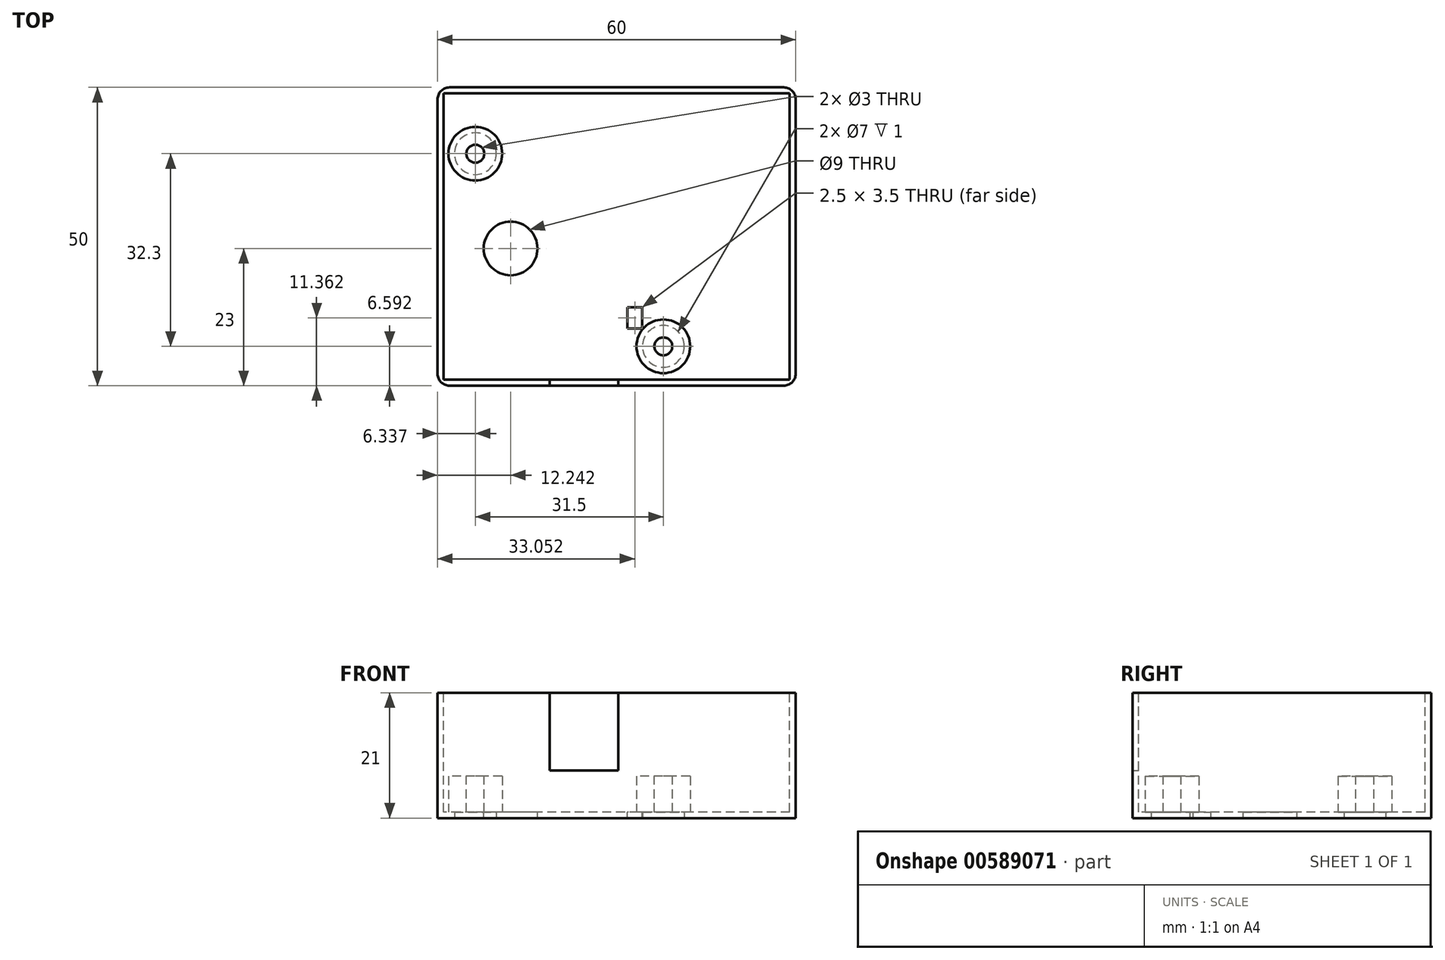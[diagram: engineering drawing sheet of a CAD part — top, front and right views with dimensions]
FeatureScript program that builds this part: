
annotation { "Feature Type Name" : "Feature", "Feature Type Description" : "" }
export const myFeature = defineFeature(function(context is Context, id is Id, definition is map)
    precondition{}
    {
        {
            var Q0;
            Q0=qCreatedBy(makeId("Top.planeOp"),FACE);
            var sketch = newSketch(context, id + "F0", { "sketchPlane" : qUnion([Q0])});
            skLineSegment(sketch, "E0.bottom", {"start": v(-60, 50) * mm, "end": v(0, 50) * mm});
            skLineSegment(sketch, "E0.top", {"start": v(-60, 0) * mm, "end": v(0, 0) * mm});
            skLineSegment(sketch, "E0.left", {"start": v(-60, 50) * mm, "end": v(-60, 0) * mm});
            skLineSegment(sketch, "E0.right", {"start": v(0, 50) * mm, "end": v(0, 0) * mm});
            skSolve(sketch);
        }
        {
            var Q0;
            Q0=makeQuery(id+"F0.imprint","IMPRINT",FACE,{"disambiguationData":[TD([[makeQuery(id+"F0.imprint","IMPRINT",EDGE,{"derivedFrom":sQuery(id+"F0.wireOp",EDGE,"E0.bottom")}),-1.0]])]});
            extrude(context, id + "F1", {"entities" : qUnion([Q0]), "depth" : 21 * mm, "offsetDistance" : 25 * mm});
        }
        {
            var Q0;
            Q0=makeQuery(id+"F1.opExtrude","CAP_FACE",FACE,{"disambiguationData":[OSD([sQuery(id+"F0.wireOp",EDGE,"E0.bottom"),sQuery(id+"F0.wireOp",EDGE,"E0.top"),sQuery(id+"F0.wireOp",EDGE,"E0.left"),sQuery(id+"F0.wireOp",EDGE,"E0.right")])],"isStart":false});
            var sketch = newSketch(context, id + "F2", { "sketchPlane" : qUnion([Q0])});
            skLineSegment(sketch, "E1.bottom", {"start": v(-1, 49) * mm, "end": v(-59, 49) * mm});
            skLineSegment(sketch, "E1.top", {"start": v(-1, 1) * mm, "end": v(-59, 1) * mm});
            skLineSegment(sketch, "E1.left", {"start": v(-1, 49) * mm, "end": v(-1, 1) * mm});
            skLineSegment(sketch, "E1.right", {"start": v(-59, 49) * mm, "end": v(-59, 1) * mm});
            skPoint(sketch, "E1.middle", {"position": v(-30, 25) * mm});
            skPoint(sketch, "E1.middle.positionSnap0", {"position": v(-60, 25) * mm});
            skPoint(sketch, "E1.middle.positionSnap1", {"position": v(-30, 50) * mm});
            skPoint(sketch, "E1.centerSnap0", {"position": v(-60, 25) * mm});
            skPoint(sketch, "E1.centerSnap1", {"position": v(-30, 50) * mm});
            skSolve(sketch);
        }
        {
            var Q0;
            Q0=makeQuery(id+"F2.imprint","IMPRINT",FACE,{"disambiguationData":[TD([[makeQuery(id+"F2.imprint","IMPRINT",EDGE,{"derivedFrom":sQuery(id+"F2.wireOp",EDGE,"E1.bottom")}),1.0]])]});
            extrude(context, id + "F3", {"entities" : qUnion([Q0]), "operationType" : NewBodyOperationType.REMOVE, "oppositeDirection" : true, "depth" : 20 * mm, "offsetDistance" : 25 * mm});
        }
        {
            var Q0;
            Q0=makeQuery(id+"F3.boolean.opBoolean","COPY",FACE,{"derivedFrom":makeQuery(id+"F3.opExtrude","CAP_FACE",FACE,{"disambiguationData":[OSD([sQuery(id+"F2.wireOp",EDGE,"E1.bottom"),sQuery(id+"F2.wireOp",EDGE,"E1.top"),sQuery(id+"F2.wireOp",EDGE,"E1.left"),sQuery(id+"F2.wireOp",EDGE,"E1.right")])],"isStart":false})});
            var sketch = newSketch(context, id + "F4", { "sketchPlane" : qUnion([Q0])});
            skSolve(sketch);
        }
        {
            var Q0;
            Q0=makeQuery(id+"F1.opExtrude","SWEPT_EDGE",EDGE,{"disambiguationData":[OSD([sQuery(id+"F0.wireOp",EDGE,"E0.bottom"),sQuery(id+"F0.wireOp",EDGE,"E0.left")])]});
            var Q1;
            Q1=makeQuery(id+"FCYQWNy7Zb7PqlJ_1.opExtrude","SWEPT_EDGE",EDGE,{"disambiguationData":[OSD([sQuery(id+"F0qmjPTTrngIJEc_1.wireOp",EDGE,"DvuROJ63-KSk5-jzMp-zI5F-EhPobcGynQcb.top"),sQuery(id+"F0qmjPTTrngIJEc_1.wireOp",EDGE,"DvuROJ63-KSk5-jzMp-zI5F-EhPobcGynQcb.right")])]});
            var Q2;
            Q2=makeQuery(id+"FCYQWNy7Zb7PqlJ_1.opExtrude","SWEPT_EDGE",EDGE,{"disambiguationData":[OSD([sQuery(id+"F2.wireOp",EDGE,"E1.bottom"),sQuery(id+"F0qmjPTTrngIJEc_1.wireOp",EDGE,"DvuROJ63-KSk5-jzMp-zI5F-EhPobcGynQcb.bottom"),sQuery(id+"F0qmjPTTrngIJEc_1.wireOp",EDGE,"DvuROJ63-KSk5-jzMp-zI5F-EhPobcGynQcb.right")])]});
            var Q3;
            Q3=makeQuery(id+"FCYQWNy7Zb7PqlJ_1.opExtrude","SWEPT_EDGE",EDGE,{"disambiguationData":[OSD([sQuery(id+"F2.wireOp",EDGE,"E1.right"),sQuery(id+"F0qmjPTTrngIJEc_1.wireOp",EDGE,"DvuROJ63-KSk5-jzMp-zI5F-EhPobcGynQcb.top"),sQuery(id+"F0qmjPTTrngIJEc_1.wireOp",EDGE,"DvuROJ63-KSk5-jzMp-zI5F-EhPobcGynQcb.left")])]});
            var Q4;
            Q4=makeQuery(id+"FCYQWNy7Zb7PqlJ_1.opExtrude","SWEPT_EDGE",EDGE,{"disambiguationData":[OSD([sQuery(id+"F2.wireOp",EDGE,"E1.bottom"),sQuery(id+"F0qmjPTTrngIJEc_1.wireOp",EDGE,"zE6tPnLL-G540-4zGb-CKbz-ck4JLzuL5Bhh.bottom"),sQuery(id+"F0qmjPTTrngIJEc_1.wireOp",EDGE,"zE6tPnLL-G540-4zGb-CKbz-ck4JLzuL5Bhh.right")])]});
            var Q5;
            Q5=makeQuery(id+"FCYQWNy7Zb7PqlJ_1.opExtrude","SWEPT_EDGE",EDGE,{"disambiguationData":[OSD([sQuery(id+"F0qmjPTTrngIJEc_1.wireOp",EDGE,"zE6tPnLL-G540-4zGb-CKbz-ck4JLzuL5Bhh.top"),sQuery(id+"F0qmjPTTrngIJEc_1.wireOp",EDGE,"zE6tPnLL-G540-4zGb-CKbz-ck4JLzuL5Bhh.right")])]});
            var Q6;
            Q6=makeQuery(id+"FCYQWNy7Zb7PqlJ_1.opExtrude","SWEPT_EDGE",EDGE,{"disambiguationData":[OSD([sQuery(id+"F2.wireOp",EDGE,"E1.left"),sQuery(id+"F0qmjPTTrngIJEc_1.wireOp",EDGE,"zE6tPnLL-G540-4zGb-CKbz-ck4JLzuL5Bhh.top"),sQuery(id+"F0qmjPTTrngIJEc_1.wireOp",EDGE,"zE6tPnLL-G540-4zGb-CKbz-ck4JLzuL5Bhh.left")])]});
            var Q7;
            Q7=makeQuery(id+"F1.opExtrude","SWEPT_EDGE",EDGE,{"disambiguationData":[OSD([sQuery(id+"F0.wireOp",EDGE,"E0.bottom"),sQuery(id+"F0.wireOp",EDGE,"E0.right")])]});
            var Q8;
            Q8=makeQuery(id+"FCYQWNy7Zb7PqlJ_1.opExtrude","SWEPT_EDGE",EDGE,{"disambiguationData":[OSD([sQuery(id+"F2.wireOp",EDGE,"E1.left"),sQuery(id+"F0qmjPTTrngIJEc_1.wireOp",EDGE,"89tvnpWX-ODYg-inec-HLnJ-TwMMxXkBzffX.top"),sQuery(id+"F0qmjPTTrngIJEc_1.wireOp",EDGE,"89tvnpWX-ODYg-inec-HLnJ-TwMMxXkBzffX.left")])]});
            var Q9;
            Q9=makeQuery(id+"FCYQWNy7Zb7PqlJ_1.opExtrude","SWEPT_EDGE",EDGE,{"disambiguationData":[OSD([sQuery(id+"F0qmjPTTrngIJEc_1.wireOp",EDGE,"89tvnpWX-ODYg-inec-HLnJ-TwMMxXkBzffX.top"),sQuery(id+"F0qmjPTTrngIJEc_1.wireOp",EDGE,"89tvnpWX-ODYg-inec-HLnJ-TwMMxXkBzffX.right")])]});
            var Q10;
            Q10=makeQuery(id+"FCYQWNy7Zb7PqlJ_1.opExtrude","SWEPT_EDGE",EDGE,{"disambiguationData":[OSD([sQuery(id+"F2.wireOp",EDGE,"E1.top"),sQuery(id+"F0qmjPTTrngIJEc_1.wireOp",EDGE,"89tvnpWX-ODYg-inec-HLnJ-TwMMxXkBzffX.bottom"),sQuery(id+"F0qmjPTTrngIJEc_1.wireOp",EDGE,"89tvnpWX-ODYg-inec-HLnJ-TwMMxXkBzffX.right")])]});
            var Q11;
            Q11=makeQuery(id+"F1.opExtrude","SWEPT_EDGE",EDGE,{"disambiguationData":[OSD([sQuery(id+"F0.wireOp",EDGE,"E0.top"),sQuery(id+"F0.wireOp",EDGE,"E0.right")])]});
            var Q12;
            Q12=makeQuery(id+"F1.opExtrude","SWEPT_EDGE",EDGE,{"disambiguationData":[OSD([sQuery(id+"F0.wireOp",EDGE,"E0.top"),sQuery(id+"F0.wireOp",EDGE,"E0.left")])]});
            var Q13;
            Q13=makeQuery(id+"FCYQWNy7Zb7PqlJ_1.opExtrude","SWEPT_EDGE",EDGE,{"disambiguationData":[OSD([sQuery(id+"F0qmjPTTrngIJEc_1.wireOp",EDGE,"9Cv9cYrh-xlaD-i3HP-BKFU-8AhRO7m4yerI.top"),sQuery(id+"F0qmjPTTrngIJEc_1.wireOp",EDGE,"9Cv9cYrh-xlaD-i3HP-BKFU-8AhRO7m4yerI.right")])]});
            var Q14;
            Q14=makeQuery(id+"FCYQWNy7Zb7PqlJ_1.opExtrude","SWEPT_EDGE",EDGE,{"disambiguationData":[OSD([sQuery(id+"F2.wireOp",EDGE,"E1.top"),sQuery(id+"F0qmjPTTrngIJEc_1.wireOp",EDGE,"9Cv9cYrh-xlaD-i3HP-BKFU-8AhRO7m4yerI.bottom"),sQuery(id+"F0qmjPTTrngIJEc_1.wireOp",EDGE,"9Cv9cYrh-xlaD-i3HP-BKFU-8AhRO7m4yerI.right")])]});
            var Q15;
            Q15=makeQuery(id+"FCYQWNy7Zb7PqlJ_1.opExtrude","SWEPT_EDGE",EDGE,{"disambiguationData":[OSD([sQuery(id+"F2.wireOp",EDGE,"E1.right"),sQuery(id+"F0qmjPTTrngIJEc_1.wireOp",EDGE,"9Cv9cYrh-xlaD-i3HP-BKFU-8AhRO7m4yerI.top"),sQuery(id+"F0qmjPTTrngIJEc_1.wireOp",EDGE,"9Cv9cYrh-xlaD-i3HP-BKFU-8AhRO7m4yerI.left")])]});
            fillet(context, id + "F5", {"entities" : qUnion([Q0, Q1, Q2, Q3, Q4, Q5, Q6, Q7, Q8, Q9, Q10, Q11, Q12, Q13, Q14, Q15]), "radius" : 2 * mm, "tangentPropagation" : true, "allowEdgeOverflow" : false});
        }
        {
            var Q0;
            Q0=makeQuery(id+"F4.imprint","IMPRINT",FACE,{"disambiguationData":[TD([[makeQuery(id+"F4.imprint","IMPRINT",EDGE,{"derivedFrom":makeQuery(id+"F3.boolean.opBoolean","COPY",EDGE,{"derivedFrom":makeQuery(id+"F3.opExtrude","CAP_EDGE",EDGE,{"disambiguationData":[OSD([sQuery(id+"F2.wireOp",EDGE,"E1.bottom")])],"isStart":false})})}),1.0]])]});
            var sketch = newSketch(context, id + "F6", { "sketchPlane" : qUnion([Q0])});
            skCircle(sketch, "E2", {"center": v(-53.66, 38.9) * mm, "radius": 4.5 * mm});
            skCircle(sketch, "E3", {"center": v(-22.16, 6.6) * mm, "radius": 4.5 * mm});
            skSolve(sketch);
        }
        {
            var Q0;
            Q0=makeQuery(id+"F6.imprint","IMPRINT",FACE,{"disambiguationData":[TD([[makeQuery(id+"F6.imprint","IMPRINT",EDGE,{"derivedFrom":sQuery(id+"F6.wireOp",EDGE,"E3")}),1.0]])]});
            var Q1;
            Q1=makeQuery(id+"F6.imprint","IMPRINT",FACE,{"disambiguationData":[TD([[makeQuery(id+"F6.imprint","IMPRINT",EDGE,{"derivedFrom":sQuery(id+"F6.wireOp",EDGE,"E2")}),1.0]])]});
            extrude(context, id + "F7", {"entities" : qUnion([Q0, Q1]), "operationType" : NewBodyOperationType.ADD, "depth" : 6 * mm, "offsetDistance" : 25 * mm});
        }
        {
            var Q0;
            Q0=makeQuery(id+"F7.opExtrude","CAP_FACE",FACE,{"disambiguationData":[OSD([sQuery(id+"F6.wireOp",EDGE,"E2")])],"isStart":false});
            var sketch = newSketch(context, id + "F8", { "sketchPlane" : qUnion([Q0])});
            skCircle(sketch, "E4", {"center": v(-53.66, 38.9) * mm, "radius": 1.5 * mm});
            skSolve(sketch);
        }
        {
            var Q0;
            Q0=makeQuery(id+"F7.opExtrude","CAP_FACE",FACE,{"disambiguationData":[OSD([sQuery(id+"F6.wireOp",EDGE,"E3")])],"isStart":false});
            var sketch = newSketch(context, id + "F9", { "sketchPlane" : qUnion([Q0])});
            skCircle(sketch, "E5", {"center": v(-22.16, 6.6) * mm, "radius": 1.5 * mm});
            skSolve(sketch);
        }
        {
            var Q0;
            Q0=makeQuery(id+"F1.opExtrude","CAP_FACE",FACE,{"disambiguationData":[OSD([sQuery(id+"F0.wireOp",EDGE,"E0.bottom"),sQuery(id+"F0.wireOp",EDGE,"E0.top"),sQuery(id+"F0.wireOp",EDGE,"E0.left"),sQuery(id+"F0.wireOp",EDGE,"E0.right")])],"isStart":false});
            var sketch = newSketch(context, id + "F10", { "sketchPlane" : qUnion([Q0])});
            skLineSegment(sketch, "E6.bottom", {"start": v(-29.73, 0) * mm, "end": v(-41.23, 0) * mm});
            skLineSegment(sketch, "E6.top", {"start": v(-29.73, 1) * mm, "end": v(-41.23, 1) * mm});
            skLineSegment(sketch, "E6.left", {"start": v(-29.73, 0) * mm, "end": v(-29.73, 1) * mm});
            skLineSegment(sketch, "E6.right", {"start": v(-41.23, 0) * mm, "end": v(-41.23, 1) * mm});
            skSolve(sketch);
        }
        {
            var Q0;
            Q0=makeQuery(id+"F10.imprint","IMPRINT",FACE,{"disambiguationData":[TD([[makeQuery(id+"F10.imprint","IMPRINT",EDGE,{"derivedFrom":sQuery(id+"F10.wireOp",EDGE,"E6.bottom")}),1.0]])]});
            extrude(context, id + "F11", {"entities" : qUnion([Q0]), "operationType" : NewBodyOperationType.REMOVE, "oppositeDirection" : true, "depth" : 13 * mm, "offsetDistance" : 25 * mm});
        }
        {
            var Q0;
            Q0=makeQuery(id+"F4.imprint","IMPRINT",FACE,{"disambiguationData":[TD([[makeQuery(id+"F4.imprint","IMPRINT",EDGE,{"derivedFrom":makeQuery(id+"F3.boolean.opBoolean","COPY",EDGE,{"derivedFrom":makeQuery(id+"F3.opExtrude","CAP_EDGE",EDGE,{"disambiguationData":[OSD([sQuery(id+"F2.wireOp",EDGE,"E1.bottom")])],"isStart":false})})}),1.0]])]});
            var sketch = newSketch(context, id + "F12", { "sketchPlane" : qUnion([Q0])});
            skLineSegment(sketch, "E7.bottom", {"start": v(-25.7, 9.61) * mm, "end": v(-28.2, 9.61) * mm});
            skLineSegment(sketch, "E7.top", {"start": v(-25.7, 13.11) * mm, "end": v(-28.2, 13.11) * mm});
            skLineSegment(sketch, "E7.left", {"start": v(-25.7, 9.61) * mm, "end": v(-25.7, 13.11) * mm});
            skLineSegment(sketch, "E7.right", {"start": v(-28.2, 9.61) * mm, "end": v(-28.2, 13.11) * mm});
            skSolve(sketch);
        }
        {
            var Q0;
            Q0=makeQuery(id+"F12.imprint","IMPRINT",FACE,{"disambiguationData":[TD([[makeQuery(id+"F12.imprint","IMPRINT",EDGE,{"derivedFrom":sQuery(id+"F12.wireOp",EDGE,"E7.bottom")}),-1.0]])]});
            extrude(context, id + "F13", {"entities" : qUnion([Q0]), "operationType" : NewBodyOperationType.REMOVE, "oppositeDirection" : true, "depth" : 1 * mm, "offsetDistance" : 25 * mm});
        }
        {
            var Q0;
            Q0=makeQuery(id+"F4.imprint","IMPRINT",FACE,{"disambiguationData":[TD([[makeQuery(id+"F4.imprint","IMPRINT",EDGE,{"derivedFrom":makeQuery(id+"F3.boolean.opBoolean","COPY",EDGE,{"derivedFrom":makeQuery(id+"F3.opExtrude","CAP_EDGE",EDGE,{"disambiguationData":[OSD([sQuery(id+"F2.wireOp",EDGE,"E1.bottom")])],"isStart":false})})}),1.0]])]});
            var sketch = newSketch(context, id + "F14", { "sketchPlane" : qUnion([Q0])});
            skCircle(sketch, "E8", {"center": v(-47.76, 23) * mm, "radius": 4.5 * mm});
            skSolve(sketch);
        }
        {
            var Q0;
            Q0=makeQuery(id+"F14.imprint","IMPRINT",FACE,{"disambiguationData":[TD([[makeQuery(id+"F14.imprint","IMPRINT",EDGE,{"derivedFrom":sQuery(id+"F14.wireOp",EDGE,"E8")}),1.0]])]});
            extrude(context, id + "F15", {"entities" : qUnion([Q0]), "operationType" : NewBodyOperationType.REMOVE, "oppositeDirection" : true, "depth" : 1 * mm, "offsetDistance" : 25 * mm});
        }
        {
            var Q0;
            Q0=makeQuery(id+"F8.imprint","IMPRINT",FACE,{"disambiguationData":[TD([[makeQuery(id+"F8.imprint","IMPRINT",EDGE,{"derivedFrom":sQuery(id+"F8.wireOp",EDGE,"E4")}),1.0]])]});
            extrude(context, id + "F16", {"entities" : qUnion([Q0]), "operationType" : NewBodyOperationType.REMOVE, "oppositeDirection" : true, "depth" : 7 * mm, "offsetDistance" : 25 * mm});
        }
        {
            var Q0;
            Q0=makeQuery(id+"F9.imprint","IMPRINT",FACE,{"disambiguationData":[TD([[makeQuery(id+"F9.imprint","IMPRINT",EDGE,{"derivedFrom":sQuery(id+"F9.wireOp",EDGE,"E5")}),1.0]])]});
            var Q1;
            Q1=sQuery(id+"F9.wireOp",EDGE,"E5");
            extrude(context, id + "F17", {"entities" : qUnion([Q0]), "operationType" : NewBodyOperationType.REMOVE, "surfaceEntities" : qUnion([Q1]), "oppositeDirection" : true, "depth" : 7 * mm, "offsetDistance" : 25 * mm});
        }
        {
            var Q0;
            Q0=makeQuery(id+"F1.opExtrude","CAP_FACE",FACE,{"disambiguationData":[OSD([sQuery(id+"F0.wireOp",EDGE,"E0.bottom"),sQuery(id+"F0.wireOp",EDGE,"E0.top"),sQuery(id+"F0.wireOp",EDGE,"E0.left"),sQuery(id+"F0.wireOp",EDGE,"E0.right")])],"isStart":true});
            var sketch = newSketch(context, id + "F18", { "sketchPlane" : qUnion([Q0])});
            skCircle(sketch, "E9", {"center": v(-53.66, -38.9) * mm, "radius": 3.5 * mm});
            skCircle(sketch, "E10", {"center": v(-22.16, -6.6) * mm, "radius": 3.5 * mm});
            skSolve(sketch);
        }
        {
            var Q0;
            Q0=makeQuery(id+"F18.imprint","IMPRINT",FACE,{"disambiguationData":[TD([[makeQuery(id+"F18.imprint","IMPRINT",EDGE,{"derivedFrom":sQuery(id+"F18.wireOp",EDGE,"E10")}),1.0]])]});
            var Q1;
            Q1=makeQuery(id+"F18.imprint","IMPRINT",FACE,{"disambiguationData":[TD([[makeQuery(id+"F18.imprint","IMPRINT",EDGE,{"derivedFrom":sQuery(id+"F18.wireOp",EDGE,"E9")}),1.0]])]});
            extrude(context, id + "F19", {"entities" : qUnion([Q0, Q1]), "operationType" : NewBodyOperationType.REMOVE, "oppositeDirection" : true, "depth" : 1 * mm, "offsetDistance" : 25 * mm});
        }
    });
